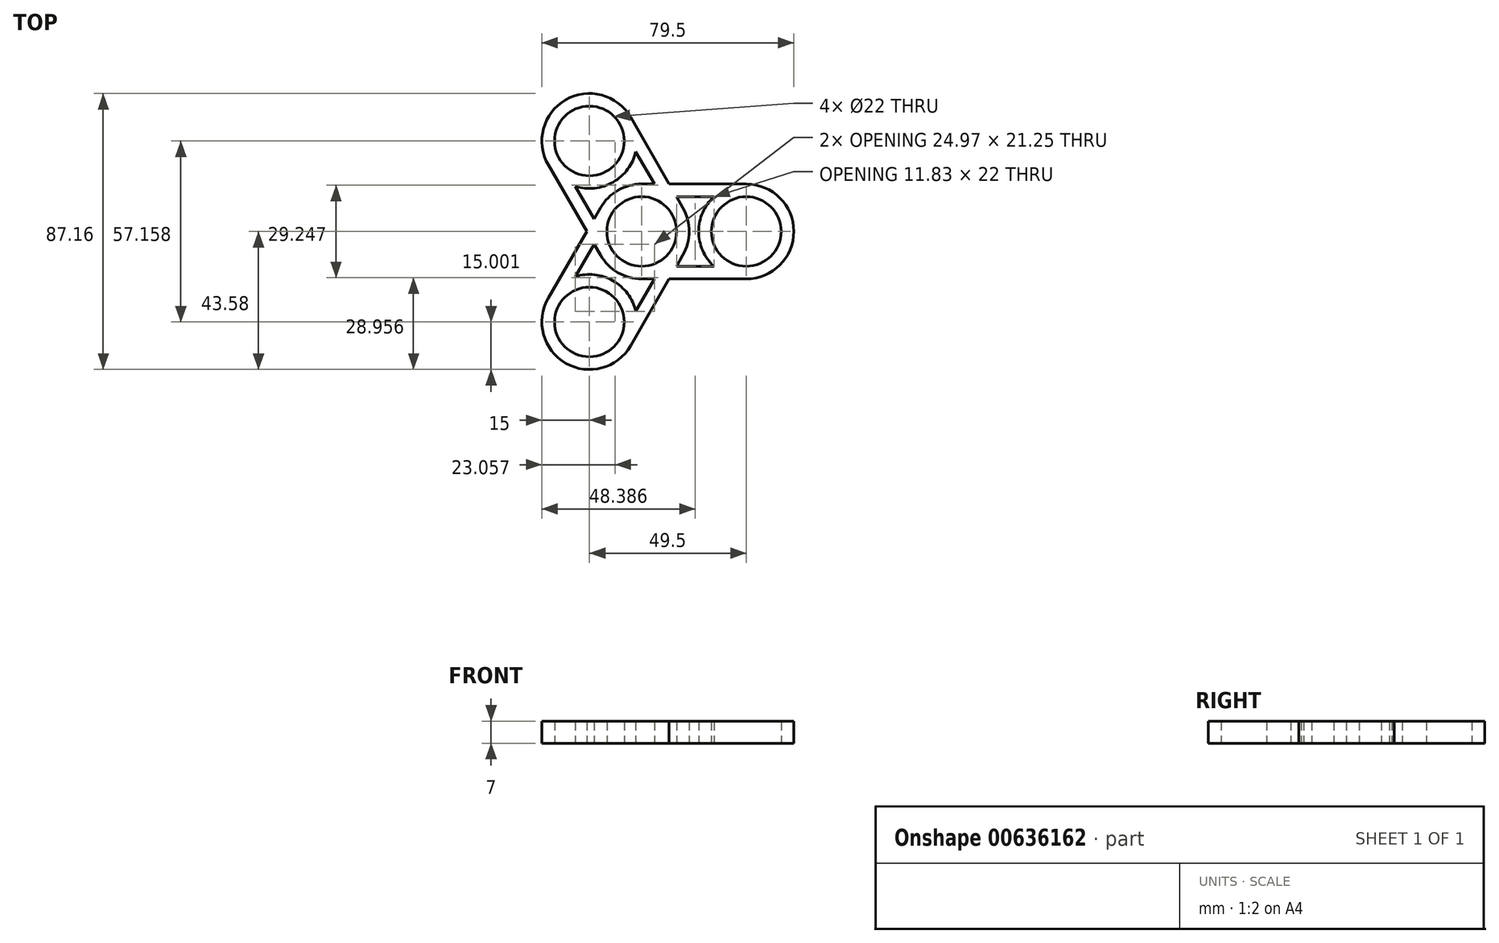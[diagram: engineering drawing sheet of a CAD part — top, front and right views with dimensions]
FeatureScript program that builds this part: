
annotation { "Feature Type Name" : "Feature", "Feature Type Description" : "" }
export const myFeature = defineFeature(function(context is Context, id is Id, definition is map)
    precondition{}
    {
        {
            var Q0;
            Q0=qCreatedBy(makeId("Top.planeOp"),FACE);
            var sketch = newSketch(context, id + "F0", { "sketchPlane" : qUnion([Q0])});
            skCircle(sketch, "E0", {"center": v(0, 0) * mm, "radius": 11 * mm});
            skArc(sketch, "E1", {"start": v(-13, -7.5) * mm, "mid": v(-7.5, -13) * mm, "end": v(0, -15) * mm});
            skCircle(sketch, "E2.1.0.0", {"center": v(33, 0) * mm, "radius": 15 * mm});
            skCircle(sketch, "E2.1.0.1", {"center": v(33, 0) * mm, "radius": 11 * mm});
            skLineSegment(sketch, "E2.direction1", {"start": v(0, 0) * mm, "end": v(33, 0) * mm, "construction": true});
            skLineSegment(sketch, "E3", {"start": v(0, 15) * mm, "end": v(4.04, 15) * mm});
            skLineSegment(sketch, "E4", {"start": v(0, -15) * mm, "end": v(4.04, -15) * mm});
            skLineSegment(sketch, "E5", {"start": v(10.97, 11) * mm, "end": v(33, 11) * mm});
            skLineSegment(sketch, "E6", {"start": v(10.97, -11) * mm, "end": v(33, -11) * mm});
            skLineSegment(sketch, "E7.1.0", {"start": v(-13, -7.5) * mm, "end": v(-15.01, -4) * mm});
            skLineSegment(sketch, "E7.1.1", {"start": v(13, 7.5) * mm, "end": v(10.97, 11) * mm});
            skLineSegment(sketch, "E7.1.2", {"start": v(-15.01, 4) * mm, "end": v(-26.03, 23.08) * mm});
            skLineSegment(sketch, "E7.1.3", {"start": v(4.04, 15) * mm, "end": v(-6.97, 34.08) * mm});
            skLineSegment(sketch, "E7.1.4", {"start": v(0, 0) * mm, "end": v(-16.5, 28.58) * mm, "construction": true});
            skCircle(sketch, "E7.1.5", {"center": v(-16.5, 28.58) * mm, "radius": 11 * mm});
            skCircle(sketch, "E7.1.6", {"center": v(-16.5, 28.58) * mm, "radius": 15 * mm});
            skLineSegment(sketch, "E7.2.0", {"start": v(13, -7.5) * mm, "end": v(10.97, -11) * mm});
            skLineSegment(sketch, "E7.2.1", {"start": v(-13, 7.5) * mm, "end": v(-15.01, 4) * mm});
            skLineSegment(sketch, "E7.2.4", {"start": v(0, 0) * mm, "end": v(-16.5, -28.58) * mm, "construction": true});
            skCircle(sketch, "E7.2.5", {"center": v(-16.5, -28.58) * mm, "radius": 11 * mm});
            skCircle(sketch, "E7.2.6", {"center": v(-16.5, -28.58) * mm, "radius": 15 * mm});
            skLineSegment(sketch, "E8.trimOffspring", {"start": v(-17.32, 0) * mm, "end": v(-29.5, 21.08) * mm});
            skLineSegment(sketch, "E9.trimOffspring", {"start": v(-17.32, 0) * mm, "end": v(-29.5, -21.08) * mm});
            skLineSegment(sketch, "E10.trimOffspring", {"start": v(-15.01, -4) * mm, "end": v(-26.03, -23.08) * mm});
            skPoint(sketch, "E11.orphan", {"position": v(-9.53, -5.5) * mm});
            skLineSegment(sketch, "E12.trimOffspring", {"start": v(4.04, -15) * mm, "end": v(-6.97, -34.08) * mm});
            skPoint(sketch, "E13.orphan", {"position": v(0, -11) * mm});
            skArc(sketch, "E14.trimOffspring", {"start": v(13, -7.5) * mm, "mid": v(15, 0) * mm, "end": v(13, 7.5) * mm});
            skLineSegment(sketch, "E15.trimOffspring", {"start": v(8.66, -15) * mm, "end": v(33, -15) * mm});
            skLineSegment(sketch, "E16.trimOffspring", {"start": v(8.66, -15) * mm, "end": v(-3.5, -36.08) * mm});
            skPoint(sketch, "E17.orphan", {"position": v(0, 11) * mm});
            skPoint(sketch, "E18.orphan", {"position": v(9.53, 5.5) * mm});
            skArc(sketch, "E19.trimOffspring", {"start": v(0, 15) * mm, "mid": v(-7.5, 13) * mm, "end": v(-13, 7.5) * mm});
            skLineSegment(sketch, "E20.trimOffspring", {"start": v(8.66, 15) * mm, "end": v(33, 15) * mm});
            skLineSegment(sketch, "E21.trimOffspring", {"start": v(8.66, 15) * mm, "end": v(-3.5, 36.08) * mm});
            skSolve(sketch);
        }
        {
            var Q0;
            Q0 = qSketchRegion(id + "F0", true);
            var Q1;
            {var subQ4=sQuery(id+"F0.wireOp",EDGE,"E6");var subQ5=sQuery(id+"F0.wireOp",EDGE,"E0");var subQ6=makeQuery(id+"F0.imprint","INTERSECT",VERTEX,{"derivedFrom":[subQ5,subQ4]});Q1=makeQuery(id+"F0.imprint","IMPRINT",FACE,{"disambiguationData":[TD([[makeQuery(id+"F0.imprint","IMPRINT",EDGE,{"disambiguationData":[TD([[subQ6,1.0]])],"derivedFrom":subQ5}),-1.0]])]});}
            var Q2;
            {var subQ0=sQuery(id+"F0.wireOp",EDGE,"E7.2.5");var subQ1=sQuery(id+"F0.wireOp",EDGE,"E7.2.2");var subQ2=makeQuery(id+"F0.imprint","INTERSECT",VERTEX,{"derivedFrom":[subQ1,subQ0]});Q2=makeQuery(id+"F0.imprint","IMPRINT",FACE,{"disambiguationData":[TD([[makeQuery(id+"F0.imprint","IMPRINT",EDGE,{"disambiguationData":[TD([[subQ2,1.0]])],"derivedFrom":subQ1}),-1.0]])]});}
            var Q3;
            {var subQ0=sQuery(id+"F0.wireOp",EDGE,"E5");var subQ1=sQuery(id+"F0.wireOp",EDGE,"E2.1.0.0");var subQ2=makeQuery(id+"F0.imprint","INTERSECT",VERTEX,{"derivedFrom":[subQ1,subQ0]});Q3=makeQuery(id+"F0.imprint","IMPRINT",FACE,{"disambiguationData":[TD([[makeQuery(id+"F0.imprint","IMPRINT",EDGE,{"disambiguationData":[TD([[subQ2,-1.0]])],"derivedFrom":subQ1}),1.0]])]});}
            var Q4;
            {var subQ7=sQuery(id+"F0.wireOp",EDGE,"E7.1.3");var subQ8=sQuery(id+"F0.wireOp",EDGE,"E0");var subQ9=makeQuery(id+"F0.imprint","INTERSECT",VERTEX,{"derivedFrom":[subQ8,subQ7]});Q4=makeQuery(id+"F0.imprint","IMPRINT",FACE,{"disambiguationData":[TD([[makeQuery(id+"F0.imprint","IMPRINT",EDGE,{"disambiguationData":[TD([[subQ9,1.0]])],"derivedFrom":subQ8}),-1.0]])]});}
            var Q5;
            {var subQ7=sQuery(id+"F0.wireOp",EDGE,"E5");var subQ8=sQuery(id+"F0.wireOp",EDGE,"E0");var subQ9=makeQuery(id+"F0.imprint","INTERSECT",VERTEX,{"derivedFrom":[subQ8,subQ7]});Q5=makeQuery(id+"F0.imprint","IMPRINT",FACE,{"disambiguationData":[TD([[makeQuery(id+"F0.imprint","IMPRINT",EDGE,{"disambiguationData":[TD([[subQ9,-1.0]])],"derivedFrom":subQ8}),-1.0]])]});}
            var Q6;
            {var subQ0=sQuery(id+"F0.wireOp",EDGE,"E7.1.5");var subQ1=sQuery(id+"F0.wireOp",EDGE,"E7.1.2");var subQ2=makeQuery(id+"F0.imprint","INTERSECT",VERTEX,{"derivedFrom":[subQ1,subQ0]});Q6=makeQuery(id+"F0.imprint","IMPRINT",FACE,{"disambiguationData":[TD([[makeQuery(id+"F0.imprint","IMPRINT",EDGE,{"disambiguationData":[TD([[subQ2,1.0]])],"derivedFrom":subQ1}),-1.0]])]});}
            var Q7;
            {var subQ0=sQuery(id+"F0.wireOp",EDGE,"E7.1.2");var subQ1=sQuery(id+"F0.wireOp",EDGE,"E1");var subQ2=makeQuery(id+"F0.imprint","INTERSECT",VERTEX,{"derivedFrom":[subQ1,subQ0]});Q7=makeQuery(id+"F0.imprint","IMPRINT",FACE,{"disambiguationData":[TD([[makeQuery(id+"F0.imprint","IMPRINT",EDGE,{"disambiguationData":[TD([[subQ2,-1.0]])],"derivedFrom":subQ1}),1.0]])]});}
            var Q8;
            {var subQ0=sQuery(id+"F0.wireOp",EDGE,"E5");var subQ1=sQuery(id+"F0.wireOp",EDGE,"E1");var subQ2=makeQuery(id+"F0.imprint","INTERSECT",VERTEX,{"derivedFrom":[subQ1,subQ0]});Q8=makeQuery(id+"F0.imprint","IMPRINT",FACE,{"disambiguationData":[TD([[makeQuery(id+"F0.imprint","IMPRINT",EDGE,{"disambiguationData":[TD([[subQ2,-1.0]])],"derivedFrom":subQ1}),1.0]])]});}
            var Q9;
            {var subQ0=sQuery(id+"F0.wireOp",EDGE,"E7.2.2");var subQ1=sQuery(id+"F0.wireOp",EDGE,"E1");var subQ2=makeQuery(id+"F0.imprint","INTERSECT",VERTEX,{"derivedFrom":[subQ1,subQ0]});Q9=makeQuery(id+"F0.imprint","IMPRINT",FACE,{"disambiguationData":[TD([[makeQuery(id+"F0.imprint","IMPRINT",EDGE,{"disambiguationData":[TD([[subQ2,-1.0]])],"derivedFrom":subQ1}),1.0]])]});}
            var Q10;
            {var subQ0=sQuery(id+"F0.wireOp",EDGE,"E6");var subQ1=sQuery(id+"F0.wireOp",EDGE,"E0");var subQ2=makeQuery(id+"F0.imprint","INTERSECT",VERTEX,{"derivedFrom":[subQ1,subQ0]});Q10=makeQuery(id+"F0.imprint","IMPRINT",FACE,{"disambiguationData":[TD([[makeQuery(id+"F0.imprint","IMPRINT",EDGE,{"disambiguationData":[TD([[subQ2,-1.0]])],"derivedFrom":subQ1}),-1.0]])]});}
            var Q11;
            {var subQ0=sQuery(id+"F0.wireOp",EDGE,"E7.1.2");var subQ1=sQuery(id+"F0.wireOp",EDGE,"E0");var subQ2=makeQuery(id+"F0.imprint","INTERSECT",VERTEX,{"derivedFrom":[subQ1,subQ0]});Q11=makeQuery(id+"F0.imprint","IMPRINT",FACE,{"disambiguationData":[TD([[makeQuery(id+"F0.imprint","IMPRINT",EDGE,{"disambiguationData":[TD([[subQ2,1.0]])],"derivedFrom":subQ1}),-1.0]])]});}
            var Q12;
            {var subQ0=sQuery(id+"F0.wireOp",EDGE,"E5");var subQ1=sQuery(id+"F0.wireOp",EDGE,"E0");var subQ2=makeQuery(id+"F0.imprint","INTERSECT",VERTEX,{"derivedFrom":[subQ1,subQ0]});Q12=makeQuery(id+"F0.imprint","IMPRINT",FACE,{"disambiguationData":[TD([[makeQuery(id+"F0.imprint","IMPRINT",EDGE,{"disambiguationData":[TD([[subQ2,1.0]])],"derivedFrom":subQ1}),-1.0]])]});}
            var Q13;
            {var subQ0=sQuery(id+"F0.wireOp",EDGE,"E10.trimOffspring");var subQ1=sQuery(id+"F0.wireOp",EDGE,"E7.2.5");var subQ2=makeQuery(id+"F0.imprint","INTERSECT",VERTEX,{"derivedFrom":[subQ1,subQ0]});Q13=makeQuery(id+"F0.imprint","IMPRINT",FACE,{"disambiguationData":[TD([[makeQuery(id+"F0.imprint","IMPRINT",EDGE,{"disambiguationData":[TD([[subQ2,1.0]])],"derivedFrom":subQ1}),-1.0]])]});}
            extrude(context, id + "F1", {"entities" : qUnion([Q0, Q1, Q2, Q3, Q4, Q5, Q6, Q7, Q8, Q9, Q10, Q11, Q12, Q13]), "depth" : 7 * mm, "offsetDistance" : 25 * mm});
        }
    });
